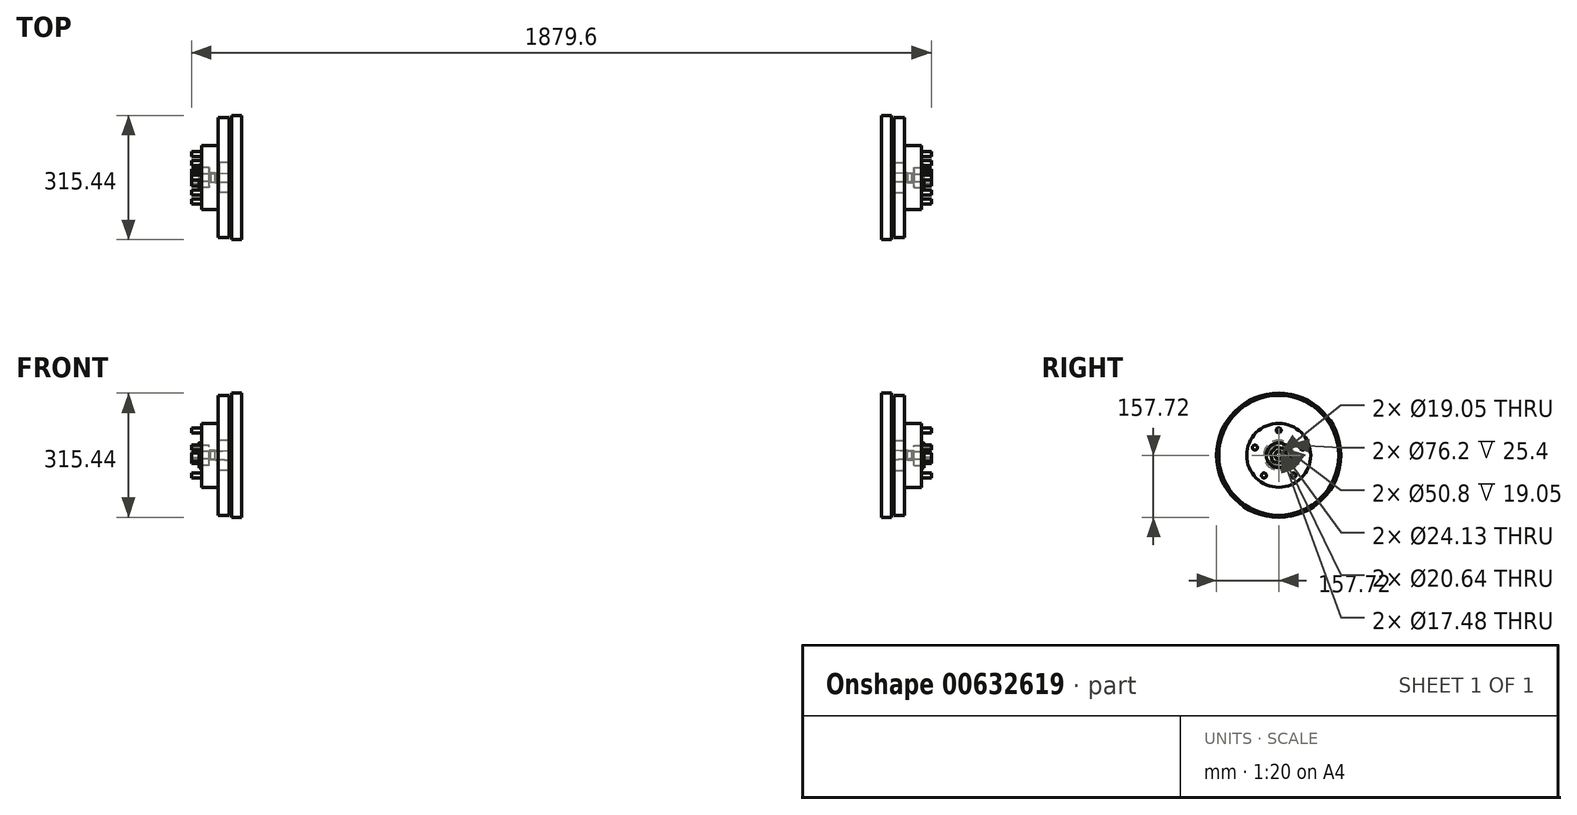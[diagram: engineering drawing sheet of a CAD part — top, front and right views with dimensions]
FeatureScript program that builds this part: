
annotation { "Feature Type Name" : "Feature", "Feature Type Description" : "" }
export const myFeature = defineFeature(function(context is Context, id is Id, definition is map)
    precondition{}
    {
        {
            var Q0;
            Q0=qCreatedBy(makeId("Top.planeOp"),FACE);
            var sketch = newSketch(context, id + "F0", { "sketchPlane" : qUnion([Q0])});
            skLineSegment(sketch, "E0.bottom", {"start": v(914.4, 0) * mm, "end": v(-914.4, 0) * mm});
            skLineSegment(sketch, "E0.top", {"start": v(914.4, 4876.8) * mm, "end": v(-914.4, 4876.8) * mm});
            skLineSegment(sketch, "E0.left", {"start": v(914.4, 0) * mm, "end": v(914.4, 4876.8) * mm});
            skLineSegment(sketch, "E0.right", {"start": v(-914.4, 0) * mm, "end": v(-914.4, 4876.8) * mm});
            skLineSegment(sketch, "E1", {"start": v(0, 4876.8) * mm, "end": v(0, 0) * mm, "construction": true});
            skSolve(sketch);
        }
        {
            var Q0;
            Q0=qCreatedBy(makeId("Front.planeOp"),FACE);
            var sketch = newSketch(context, id + "F1", { "sketchPlane" : qUnion([Q0])});
            skLineSegment(sketch, "E2", {"start": v(914.4, -25.4) * mm, "end": v(914.4, -81.22) * mm});
            skLineSegment(sketch, "E3", {"start": v(871.91, -152.4) * mm, "end": v(844.44, -152.4) * mm});
            skLineSegment(sketch, "E4", {"start": v(844.44, -152.4) * mm, "end": v(844.44, -38.1) * mm});
            skLineSegment(sketch, "E5", {"start": v(844.44, -38.1) * mm, "end": v(869.84, -38.1) * mm});
            skLineSegment(sketch, "E6", {"start": v(869.84, -38.1) * mm, "end": v(869.84, -12.25) * mm});
            skLineSegment(sketch, "E7", {"start": v(879.44, -12.06) * mm, "end": v(895.35, -12.06) * mm});
            skLineSegment(sketch, "E8", {"start": v(869.84, -12.25) * mm, "end": v(879.44, -12.06) * mm});
            skLineSegment(sketch, "E9", {"start": v(895.35, -12.06) * mm, "end": v(895.35, -25.4) * mm});
            skLineSegment(sketch, "E10", {"start": v(895.35, -25.4) * mm, "end": v(914.4, -25.4) * mm});
            skLineSegment(sketch, "E11", {"start": v(844.44, -38.1) * mm, "end": v(844.44, -11.81) * mm});
            skLineSegment(sketch, "E12", {"start": v(844.44, -11.81) * mm, "end": v(869.84, -10.56) * mm});
            skLineSegment(sketch, "E13", {"start": v(869.84, -10.56) * mm, "end": v(869.84, -12.25) * mm});
            skLineSegment(sketch, "E14", {"start": v(914.4, -25.4) * mm, "end": v(914.4, -9.52) * mm});
            skLineSegment(sketch, "E15", {"start": v(914.4, -9.52) * mm, "end": v(895.35, -9.52) * mm});
            skLineSegment(sketch, "E16", {"start": v(895.35, -9.53) * mm, "end": v(895.35, -12.06) * mm});
            skLineSegment(sketch, "E17", {"start": v(914.4, -9.52) * mm, "end": v(939.8, -9.52) * mm});
            skLineSegment(sketch, "E18", {"start": v(939.8, -9.52) * mm, "end": v(939.8, 0) * mm});
            skLineSegment(sketch, "E19", {"start": v(939.8, 0) * mm, "end": v(812.98, 0) * mm});
            skLineSegment(sketch, "E20", {"start": v(812.98, 0) * mm, "end": v(812.98, -157.72) * mm});
            skLineSegment(sketch, "E21", {"start": v(812.98, -157.72) * mm, "end": v(838.1, -157.72) * mm});
            skLineSegment(sketch, "E22", {"start": v(841.27, -18.32) * mm, "end": v(841.27, -11.97) * mm});
            skLineSegment(sketch, "E23", {"start": v(841.27, -11.97) * mm, "end": v(844.44, -11.81) * mm});
            skLineSegment(sketch, "E24", {"start": v(869.84, -10.56) * mm, "end": v(890.69, -9.52) * mm});
            skLineSegment(sketch, "E25", {"start": v(890.69, -9.52) * mm, "end": v(895.35, -9.52) * mm});
            skLineSegment(sketch, "E26.top", {"start": v(871.91, -81.22) * mm, "end": v(914.4, -81.22) * mm});
            skLineSegment(sketch, "E26.left", {"start": v(871.91, -152.4) * mm, "end": v(871.91, -81.22) * mm});
            skLineSegment(sketch, "E27", {"start": v(841.27, -18.32) * mm, "end": v(838.1, -18.32) * mm});
            skLineSegment(sketch, "E28", {"start": v(838.1, -18.32) * mm, "end": v(838.1, -157.72) * mm});
            skSolve(sketch);
        }
        {
            var Q0;
            Q0=makeQuery(id+"F1.imprint","IMPRINT",FACE,{"disambiguationData":[TD([[makeQuery(id+"F1.imprint","IMPRINT",EDGE,{"derivedFrom":sQuery(id+"F1.wireOp",EDGE,"E12")}),1.0]])]});
            var Q1;
            Q1=sQuery(id+"F1.wireOp",EDGE,"E19");
            revolve(context, id + "F2", {"entities" : qUnion([Q0]), "axis" : qUnion([Q1]), "revolveType" : RevolveType.FULL});
        }
        {
            var Q0;
            Q0=makeQuery(id+"F1.imprint","IMPRINT",FACE,{"disambiguationData":[TD([[makeQuery(id+"F1.imprint","IMPRINT",EDGE,{"derivedFrom":sQuery(id+"F1.wireOp",EDGE,"E2")}),-1.0]])]});
            var Q1;
            Q1=sQuery(id+"F1.wireOp",EDGE,"E19");
            revolve(context, id + "F3", {"entities" : qUnion([Q0]), "axis" : qUnion([Q1]), "revolveType" : RevolveType.FULL});
        }
        {
            var Q0;
            Q0=makeQuery(id+"F1.imprint","IMPRINT",FACE,{"disambiguationData":[TD([[makeQuery(id+"F1.imprint","IMPRINT",EDGE,{"derivedFrom":sQuery(id+"F1.wireOp",EDGE,"E5")}),1.0]])]});
            var Q1;
            Q1=sQuery(id+"F1.wireOp",EDGE,"E19");
            revolve(context, id + "F4", {"entities" : qUnion([Q0]), "axis" : qUnion([Q1]), "revolveType" : RevolveType.FULL});
        }
        {
            var Q0;
            Q0=makeQuery(id+"F1.imprint","IMPRINT",FACE,{"disambiguationData":[TD([[makeQuery(id+"F1.imprint","IMPRINT",EDGE,{"derivedFrom":sQuery(id+"F1.wireOp",EDGE,"E9")}),1.0]])]});
            var Q1;
            Q1=sQuery(id+"F1.wireOp",EDGE,"E19");
            revolve(context, id + "F5", {"entities" : qUnion([Q0]), "axis" : qUnion([Q1]), "revolveType" : RevolveType.FULL});
        }
        {
            var Q0;
            Q0=makeQuery(id+"F3.opRevolve","SWEPT_FACE",FACE,{"disambiguationData":[OSD([sQuery(id+"F1.wireOp",EDGE,"E2")])]});
            var sketch = newSketch(context, id + "F6", { "sketchPlane" : qUnion([Q0])});
            skCircle(sketch, "E29", {"center": v(0, 63.5) * mm, "radius": 6.35 * mm});
            skCircle(sketch, "E30.1.0", {"center": v(-60.4, 19.62) * mm, "radius": 6.35 * mm});
            skCircle(sketch, "E30.2.0", {"center": v(-37.32, -51.37) * mm, "radius": 6.35 * mm});
            skCircle(sketch, "E30.3.0", {"center": v(37.32, -51.37) * mm, "radius": 6.35 * mm});
            skCircle(sketch, "E30.4.0", {"center": v(60.4, 19.62) * mm, "radius": 6.35 * mm});
            skPoint(sketch, "E30.center", {"position": v(0, 0) * mm});
            skSolve(sketch);
        }
        {
            var Q0;
            Q0 = qSketchRegion(id + "F6", true);
            extrude(context, id + "F7", {"entities" : qUnion([Q0]), "operationType" : NewBodyOperationType.ADD, "depth" : 25.4 * mm, "offsetDistance" : 25.4 * mm});
        }
        {
            var Q0;
            Q0=makeQuery(id+"F3.opRevolve","SWEPT_FACE",FACE,{"disambiguationData":[OSD([sQuery(id+"F1.wireOp",EDGE,"E2")])]});
            var sketch = newSketch(context, id + "F8", { "sketchPlane" : qUnion([Q0])});
            skCircle(sketch, "E31", {"center": v(0, 0) * mm, "radius": 31.75 * mm});
            skCircle(sketch, "E32", {"center": v(0, 0) * mm, "radius": 10.32 * mm});
            skSolve(sketch);
        }
        {
            var Q0;
            Q0 = qSketchRegion(id + "F8", true);
            extrude(context, id + "F9", {"entities" : qUnion([Q0]), "depth" : 6.35 * mm, "offsetDistance" : 25.4 * mm});
        }
        {
            var Q0;
            Q0=makeQuery(id+"F9.opExtrude","CAP_FACE",FACE,{"disambiguationData":[OSD([sQuery(id+"F8.wireOp",EDGE,"E31"),sQuery(id+"F8.wireOp",EDGE,"E32")])],"isStart":false});
            var sketch = newSketch(context, id + "F10", { "sketchPlane" : qUnion([Q0])});
            skCircle(sketch, "E33", {"center": v(0, 0) * mm, "radius": 8.74 * mm});
            skCircle(sketch, "E34.cCircle", {"center": v(0, 0) * mm, "radius": 19.05 * mm, "construction": true});
            skLineSegment(sketch, "E34.0", {"start": v(-5.77, 21.23) * mm, "end": v(15.5, 15.6) * mm});
            skLineSegment(sketch, "E34.1", {"start": v(15.5, 15.6) * mm, "end": v(21.27, -5.62) * mm});
            skLineSegment(sketch, "E34.2", {"start": v(21.27, -5.62) * mm, "end": v(5.77, -21.23) * mm});
            skLineSegment(sketch, "E34.3", {"start": v(5.77, -21.23) * mm, "end": v(-15.5, -15.6) * mm});
            skLineSegment(sketch, "E34.4", {"start": v(-15.5, -15.6) * mm, "end": v(-21.27, 5.62) * mm});
            skLineSegment(sketch, "E34.5", {"start": v(-21.27, 5.62) * mm, "end": v(-5.77, 21.23) * mm});
            skPoint(sketch, "E34.0.midPoint", {"position": v(4.87, 18.42) * mm});
            skSolve(sketch);
        }
        {
            var Q0;
            Q0 = qSketchRegion(id + "F10", true);
            extrude(context, id + "F11", {"entities" : qUnion([Q0]), "depth" : 19.05 * mm, "offsetDistance" : 25.4 * mm});
        }
        {
            var Q0;
            Q0=makeQuery(id+"F2.opRevolve","SWEPT_BODY",BODY,{"disambiguationData":[OSD([sQuery(id+"F1.wireOp",EDGE,"E12"),sQuery(id+"F1.wireOp",EDGE,"E15"),sQuery(id+"F1.wireOp",EDGE,"E17"),sQuery(id+"F1.wireOp",EDGE,"E18"),sQuery(id+"F1.wireOp",EDGE,"E19"),sQuery(id+"F1.wireOp",EDGE,"E20"),sQuery(id+"F1.wireOp",EDGE,"E21"),sQuery(id+"F1.wireOp",EDGE,"E22"),sQuery(id+"F1.wireOp",EDGE,"E23"),sQuery(id+"F1.wireOp",EDGE,"E24"),sQuery(id+"F1.wireOp",EDGE,"E25"),sQuery(id+"F1.wireOp",EDGE,"E27"),sQuery(id+"F1.wireOp",EDGE,"E28")])]});
            var Q1;
            Q1=makeQuery(id+"F3.opRevolve","SWEPT_BODY",BODY,{"disambiguationData":[OSD([sQuery(id+"F1.wireOp",EDGE,"E2"),sQuery(id+"F1.wireOp",EDGE,"E3"),sQuery(id+"F1.wireOp",EDGE,"E4"),sQuery(id+"F1.wireOp",EDGE,"E5"),sQuery(id+"F1.wireOp",EDGE,"E6"),sQuery(id+"F1.wireOp",EDGE,"E7"),sQuery(id+"F1.wireOp",EDGE,"E8"),sQuery(id+"F1.wireOp",EDGE,"E9"),sQuery(id+"F1.wireOp",EDGE,"E10"),sQuery(id+"F1.wireOp",EDGE,"E26.top"),sQuery(id+"F1.wireOp",EDGE,"E26.left")])]});
            var Q2;
            Q2=makeQuery(id+"F4.opRevolve","SWEPT_BODY",BODY,{"disambiguationData":[OSD([sQuery(id+"F1.wireOp",EDGE,"E5"),sQuery(id+"F1.wireOp",EDGE,"E6"),sQuery(id+"F1.wireOp",EDGE,"E11"),sQuery(id+"F1.wireOp",EDGE,"E12"),sQuery(id+"F1.wireOp",EDGE,"E13")])]});
            var Q3;
            Q3=makeQuery(id+"F5.opRevolve","SWEPT_BODY",BODY,{"disambiguationData":[OSD([sQuery(id+"F1.wireOp",EDGE,"E9"),sQuery(id+"F1.wireOp",EDGE,"E10"),sQuery(id+"F1.wireOp",EDGE,"E14"),sQuery(id+"F1.wireOp",EDGE,"E15"),sQuery(id+"F1.wireOp",EDGE,"E16")])]});
            var Q4;
            Q4=makeQuery(id+"F9.opExtrude","SWEPT_BODY",BODY,{"disambiguationData":[OSD([sQuery(id+"F8.wireOp",EDGE,"E31"),sQuery(id+"F8.wireOp",EDGE,"E32")])]});
            var Q5;
            Q5=makeQuery(id+"F11.opExtrude","SWEPT_BODY",BODY,{"disambiguationData":[OSD([sQuery(id+"F10.wireOp",EDGE,"E33"),sQuery(id+"F10.wireOp",EDGE,"E34.0"),sQuery(id+"F10.wireOp",EDGE,"E34.1"),sQuery(id+"F10.wireOp",EDGE,"E34.2"),sQuery(id+"F10.wireOp",EDGE,"E34.3"),sQuery(id+"F10.wireOp",EDGE,"E34.4"),sQuery(id+"F10.wireOp",EDGE,"E34.5")])]});
            var Q6;
            Q6=qCreatedBy(makeId("Right.planeOp"),FACE);
            mirror(context, id + "F12", {"entities" : qUnion([Q0, Q1, Q2, Q3, Q4, Q5]), "mirrorPlane" : qUnion([Q6])});
        }
        {
            var Q0;
            Q0=makeQuery(id+"F2.opRevolve","SWEPT_BODY",BODY,{"disambiguationData":[OSD([sQuery(id+"F1.wireOp",EDGE,"E12"),sQuery(id+"F1.wireOp",EDGE,"E15"),sQuery(id+"F1.wireOp",EDGE,"E17"),sQuery(id+"F1.wireOp",EDGE,"E18"),sQuery(id+"F1.wireOp",EDGE,"E19"),sQuery(id+"F1.wireOp",EDGE,"E20"),sQuery(id+"F1.wireOp",EDGE,"E21"),sQuery(id+"F1.wireOp",EDGE,"E22"),sQuery(id+"F1.wireOp",EDGE,"E23"),sQuery(id+"F1.wireOp",EDGE,"E24"),sQuery(id+"F1.wireOp",EDGE,"E25"),sQuery(id+"F1.wireOp",EDGE,"E27"),sQuery(id+"F1.wireOp",EDGE,"E28")])]});
            var Q1;
            Q1=makeQuery(id+"F0.imprint","IMPRINT",FACE,{"disambiguationData":[TD([[makeQuery(id+"F0.imprint","IMPRINT",EDGE,{"derivedFrom":sQuery(id+"F0.wireOp",EDGE,"E0.bottom")}),-1.0]])]});
            mirror(context, id + "F14", {"entities" : qUnion([Q0]), "mirrorPlane" : qUnion([Q1])});
        }
    });
